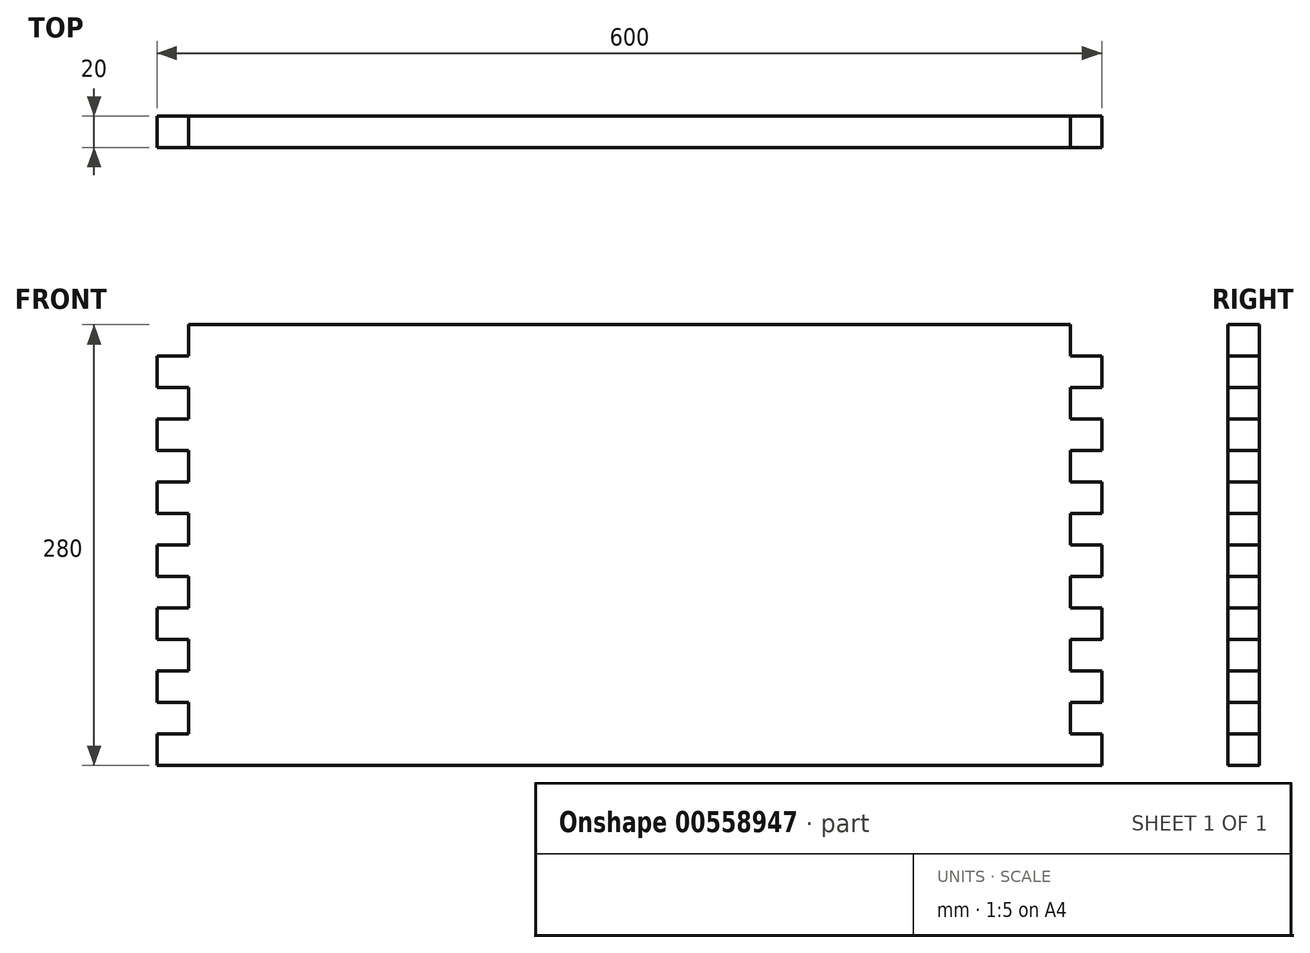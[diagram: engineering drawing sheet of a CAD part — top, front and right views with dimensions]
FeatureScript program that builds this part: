
annotation { "Feature Type Name" : "Feature", "Feature Type Description" : "" }
export const myFeature = defineFeature(function(context is Context, id is Id, definition is map)
    precondition{}
    {
        {
            var Q0;
            Q0=qCreatedBy(makeId("Front.planeOp"),FACE);
            var sketch = newSketch(context, id + "F0", { "sketchPlane" : qUnion([Q0])});
            skLineSegment(sketch, "E0.bottom", {"start": v(300, -140) * mm, "end": v(-300, -140) * mm});
            skLineSegment(sketch, "E0.top", {"start": v(300, 140) * mm, "end": v(-300, 140) * mm});
            skLineSegment(sketch, "E0.left", {"start": v(300, -140) * mm, "end": v(300, 140) * mm});
            skLineSegment(sketch, "E0.right", {"start": v(-300, -140) * mm, "end": v(-300, 140) * mm});
            skPoint(sketch, "E0.middle", {"position": v(0, 0) * mm});
            skSolve(sketch);
        }
        {
            var Q0;
            Q0=makeQuery(id+"F0.imprint","IMPRINT",FACE,{"disambiguationData":[TD([[makeQuery(id+"F0.imprint","IMPRINT",EDGE,{"derivedFrom":sQuery(id+"F0.wireOp",EDGE,"E0.bottom")}),-1.0]])]});
            extrude(context, id + "F1", {"entities" : qUnion([Q0]), "depth" : 20 * mm, "offsetDistance" : 25 * mm});
        }
        {
            var Q0;
            Q0=makeQuery(id+"F1.opExtrude","CAP_FACE",FACE,{"disambiguationData":[OSD([sQuery(id+"F0.wireOp",EDGE,"E0.bottom"),sQuery(id+"F0.wireOp",EDGE,"E0.top"),sQuery(id+"F0.wireOp",EDGE,"E0.left"),sQuery(id+"F0.wireOp",EDGE,"E0.right")])],"isStart":false});
            var sketch = newSketch(context, id + "F2", { "sketchPlane" : qUnion([Q0])});
            skLineSegment(sketch, "E1.bottom", {"start": v(-300, -120) * mm, "end": v(-280, -120) * mm});
            skLineSegment(sketch, "E1.top", {"start": v(-300, -100) * mm, "end": v(-280, -100) * mm});
            skLineSegment(sketch, "E1.left", {"start": v(-300, -120) * mm, "end": v(-300, -100) * mm});
            skLineSegment(sketch, "E1.right", {"start": v(-280, -120) * mm, "end": v(-280, -100) * mm});
            skLineSegment(sketch, "E2.0.1.0", {"start": v(-280, -80) * mm, "end": v(-280, -60) * mm});
            skLineSegment(sketch, "E2.0.1.1", {"start": v(-300, -80) * mm, "end": v(-300, -60) * mm});
            skLineSegment(sketch, "E2.0.1.2", {"start": v(-300, -60) * mm, "end": v(-280, -60) * mm});
            skLineSegment(sketch, "E2.0.1.3", {"start": v(-300, -80) * mm, "end": v(-280, -80) * mm});
            skLineSegment(sketch, "E2.0.2.0", {"start": v(-280, -40) * mm, "end": v(-280, -20) * mm});
            skLineSegment(sketch, "E2.0.2.1", {"start": v(-300, -40) * mm, "end": v(-300, -20) * mm});
            skLineSegment(sketch, "E2.0.2.2", {"start": v(-300, -20) * mm, "end": v(-280, -20) * mm});
            skLineSegment(sketch, "E2.0.2.3", {"start": v(-300, -40) * mm, "end": v(-280, -40) * mm});
            skLineSegment(sketch, "E2.0.3.0", {"start": v(-280, 0) * mm, "end": v(-280, 20) * mm});
            skLineSegment(sketch, "E2.0.3.1", {"start": v(-300, 0) * mm, "end": v(-300, 20) * mm});
            skLineSegment(sketch, "E2.0.3.2", {"start": v(-300, 20) * mm, "end": v(-280, 20) * mm});
            skLineSegment(sketch, "E2.0.3.3", {"start": v(-300, 0) * mm, "end": v(-280, 0) * mm});
            skLineSegment(sketch, "E2.0.4.0", {"start": v(-280, 40) * mm, "end": v(-280, 60) * mm});
            skLineSegment(sketch, "E2.0.4.1", {"start": v(-300, 40) * mm, "end": v(-300, 60) * mm});
            skLineSegment(sketch, "E2.0.4.2", {"start": v(-300, 60) * mm, "end": v(-280, 60) * mm});
            skLineSegment(sketch, "E2.0.4.3", {"start": v(-300, 40) * mm, "end": v(-280, 40) * mm});
            skLineSegment(sketch, "E2.0.5.0", {"start": v(-280, 80) * mm, "end": v(-280, 100) * mm});
            skLineSegment(sketch, "E2.0.5.1", {"start": v(-300, 80) * mm, "end": v(-300, 100) * mm});
            skLineSegment(sketch, "E2.0.5.2", {"start": v(-300, 100) * mm, "end": v(-280, 100) * mm});
            skLineSegment(sketch, "E2.0.5.3", {"start": v(-300, 80) * mm, "end": v(-280, 80) * mm});
            skLineSegment(sketch, "E2.0.6.0", {"start": v(-280, 120) * mm, "end": v(-280, 140) * mm});
            skLineSegment(sketch, "E2.0.6.1", {"start": v(-300, 120) * mm, "end": v(-300, 140) * mm});
            skLineSegment(sketch, "E2.0.6.2", {"start": v(-300, 140) * mm, "end": v(-280, 140) * mm});
            skLineSegment(sketch, "E2.0.6.3", {"start": v(-300, 120) * mm, "end": v(-280, 120) * mm});
            skLineSegment(sketch, "E2.direction1", {"start": v(-300, -120) * mm, "end": v(-275, -120) * mm, "construction": true});
            skLineSegment(sketch, "E2.direction2", {"start": v(-300, -120) * mm, "end": v(-300, -80) * mm, "construction": true});
            skLineSegment(sketch, "E3.MirrorCS", {"start": v(300, -120) * mm, "end": v(280, -120) * mm});
            skLineSegment(sketch, "E4.MirrorCS", {"start": v(300, -120) * mm, "end": v(300, -80) * mm, "construction": true});
            skLineSegment(sketch, "E5.MirrorCS", {"start": v(300, -120) * mm, "end": v(275, -120) * mm, "construction": true});
            skLineSegment(sketch, "E6.MirrorCS", {"start": v(300, -120) * mm, "end": v(300, -100) * mm});
            skLineSegment(sketch, "E7.MirrorCS", {"start": v(280, 40) * mm, "end": v(280, 60) * mm});
            skLineSegment(sketch, "E8.MirrorCS", {"start": v(280, 80) * mm, "end": v(280, 100) * mm});
            skLineSegment(sketch, "E9.MirrorCS", {"start": v(300, 80) * mm, "end": v(280, 80) * mm});
            skLineSegment(sketch, "E10.MirrorCS", {"start": v(300, 120) * mm, "end": v(280, 120) * mm});
            skLineSegment(sketch, "E11.MirrorCS", {"start": v(280, 120) * mm, "end": v(280, 140) * mm});
            skLineSegment(sketch, "E12.MirrorCS", {"start": v(300, 80) * mm, "end": v(300, 100) * mm});
            skLineSegment(sketch, "E13.MirrorCS", {"start": v(300, 40) * mm, "end": v(300, 60) * mm});
            skLineSegment(sketch, "E14.MirrorCS", {"start": v(300, 0) * mm, "end": v(300, 20) * mm});
            skLineSegment(sketch, "E15.MirrorCS", {"start": v(300, 140) * mm, "end": v(280, 140) * mm});
            skLineSegment(sketch, "E16.MirrorCS", {"start": v(300, 40) * mm, "end": v(280, 40) * mm});
            skLineSegment(sketch, "E17.MirrorCS", {"start": v(300, 20) * mm, "end": v(280, 20) * mm});
            skLineSegment(sketch, "E18.MirrorCS", {"start": v(300, 0) * mm, "end": v(280, 0) * mm});
            skLineSegment(sketch, "E19.MirrorCS", {"start": v(300, -100) * mm, "end": v(280, -100) * mm});
            skLineSegment(sketch, "E20.MirrorCS", {"start": v(280, -120) * mm, "end": v(280, -100) * mm});
            skLineSegment(sketch, "E21.MirrorCS", {"start": v(280, -80) * mm, "end": v(280, -60) * mm});
            skLineSegment(sketch, "E22.MirrorCS", {"start": v(300, -80) * mm, "end": v(300, -60) * mm});
            skLineSegment(sketch, "E23.MirrorCS", {"start": v(300, -60) * mm, "end": v(280, -60) * mm});
            skLineSegment(sketch, "E24.MirrorCS", {"start": v(300, -80) * mm, "end": v(280, -80) * mm});
            skLineSegment(sketch, "E25.MirrorCS", {"start": v(280, -40) * mm, "end": v(280, -20) * mm});
            skLineSegment(sketch, "E26.MirrorCS", {"start": v(300, -40) * mm, "end": v(300, -20) * mm});
            skLineSegment(sketch, "E27.MirrorCS", {"start": v(300, -20) * mm, "end": v(280, -20) * mm});
            skLineSegment(sketch, "E28.MirrorCS", {"start": v(300, 100) * mm, "end": v(280, 100) * mm});
            skLineSegment(sketch, "E29.MirrorCS", {"start": v(280, 0) * mm, "end": v(280, 20) * mm});
            skLineSegment(sketch, "E30.MirrorCS", {"start": v(300, 120) * mm, "end": v(300, 140) * mm});
            skLineSegment(sketch, "E31.MirrorCS", {"start": v(300, -40) * mm, "end": v(280, -40) * mm});
            skLineSegment(sketch, "E32.MirrorCS", {"start": v(300, 60) * mm, "end": v(280, 60) * mm});
            skSolve(sketch);
        }
        {
            var Q0;
            Q0 = qSketchRegion(id + "F2", true);
            extrude(context, id + "F3", {"entities" : qUnion([Q0]), "operationType" : NewBodyOperationType.REMOVE, "endBound" : BoundingType.UP_TO_NEXT, "oppositeDirection" : true, "depth" : 25 * mm, "offsetDistance" : 25 * mm});
        }
    });
